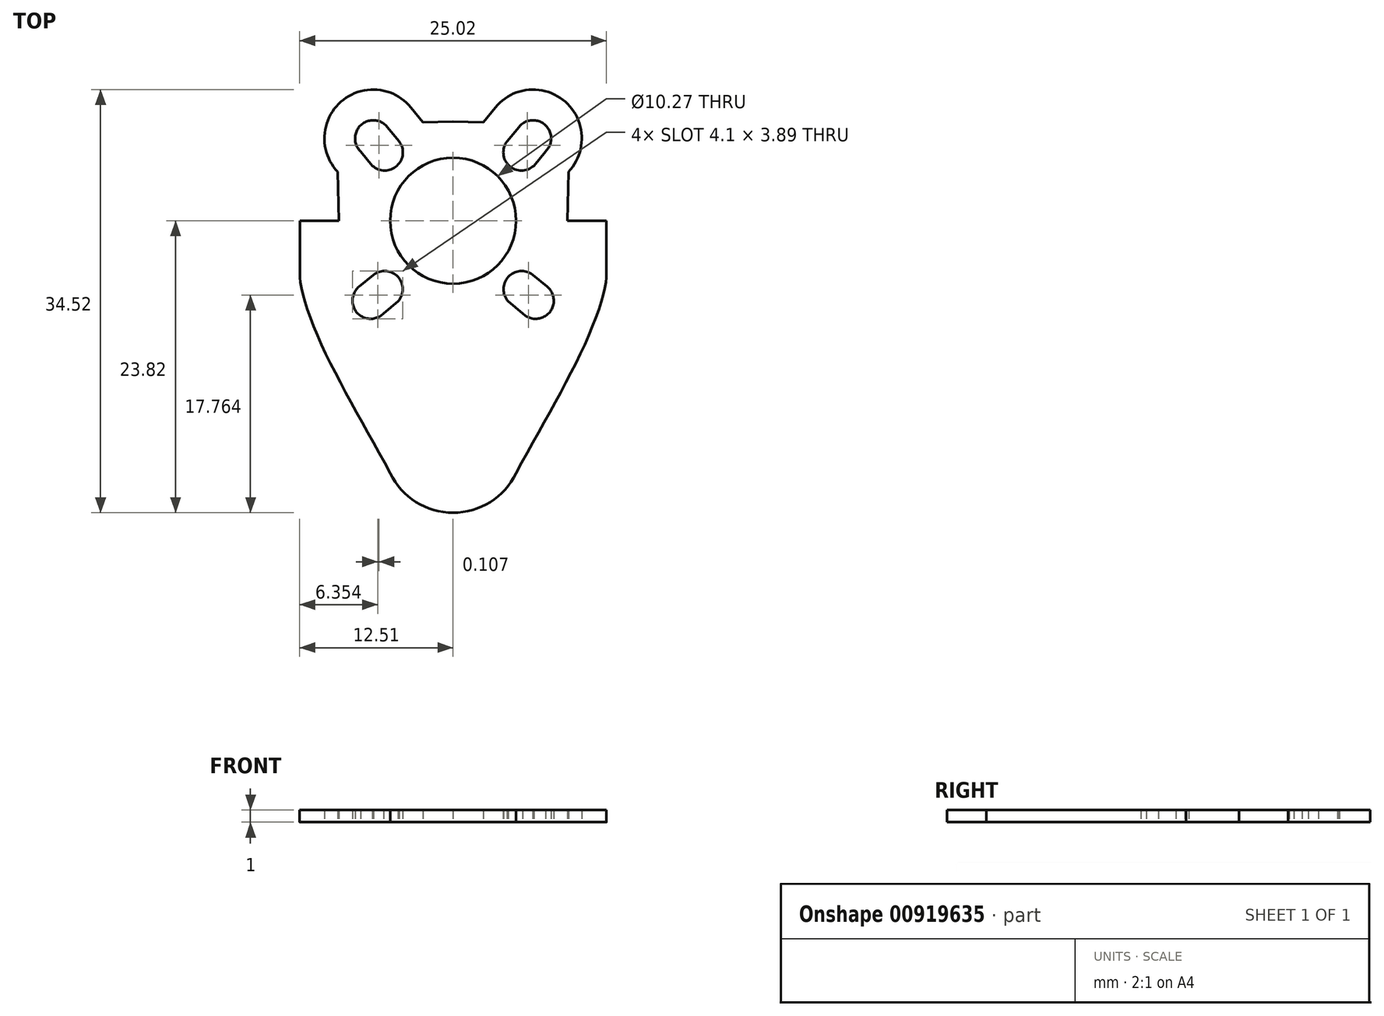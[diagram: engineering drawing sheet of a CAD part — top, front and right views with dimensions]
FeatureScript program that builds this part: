
annotation { "Feature Type Name" : "Feature", "Feature Type Description" : "" }
export const myFeature = defineFeature(function(context is Context, id is Id, definition is map)
    precondition{}
    {
        {
            var Q0;
            Q0=qCreatedBy(makeId("Top.planeOp"),FACE);
            var sketch = newSketch(context, id + "F0", { "sketchPlane" : qUnion([Q0])});
            skArc(sketch, "E0", {"start": v(-5.15, -20.56) * mm, "mid": v(-3.05, -22.94) * mm, "end": v(0, -23.82) * mm});
            skLineSegment(sketch, "E1.bottom", {"start": v(0, 0) * mm, "end": v(-12.5, 0) * mm});
            skLineSegment(sketch, "E1.right", {"start": v(-12.5, 0) * mm, "end": v(-12.5, -4.33) * mm});
            skPoint(sketch, "E1.middle", {"position": v(0, 0) * mm});
            skFitSpline(sketch, "E2", {"points": [v(-12.5, -4.33) * mm, v(-11.08, -9.31) * mm, v(-5.13, -20.6) * mm, v(-5.15, -20.56) * mm], "startDerivative": vector(-0.72, -6.32) * mm, "endDerivative": vector(-22.78, 42.97) * mm});
            skLineSegment(sketch, "E3", {"start": v(0, 0) * mm, "end": v(0, -23.82) * mm});
            skArc(sketch, "E4", {"start": v(-4.5, -6.58) * mm, "mid": v(-4.5, -4.58) * mm, "end": v(-6.49, -4.41) * mm});
            skArc(sketch, "E5", {"start": v(-7.67, -5.38) * mm, "mid": v(-7.82, -7.53) * mm, "end": v(-5.67, -7.55) * mm});
            skLineSegment(sketch, "E6", {"start": v(-6.49, -4.41) * mm, "end": v(-7.67, -5.38) * mm});
            skLineSegment(sketch, "E7", {"start": v(-5.67, -7.55) * mm, "end": v(-4.5, -6.58) * mm});
            skLineSegment(sketch, "E8.0", {"start": v(-14.38, 0) * mm, "end": v(-14.38, -4.33) * mm});
            skArc(sketch, "E9", {"start": v(-6.58, 4.49) * mm, "mid": v(-4.58, 4.49) * mm, "end": v(-4.4, 6.48) * mm});
            skArc(sketch, "E10", {"start": v(-5.37, 7.66) * mm, "mid": v(-7.52, 7.8) * mm, "end": v(-7.55, 5.66) * mm});
            skLineSegment(sketch, "E11", {"start": v(-4.4, 6.48) * mm, "end": v(-5.37, 7.66) * mm});
            skLineSegment(sketch, "E12", {"start": v(-7.55, 5.66) * mm, "end": v(-6.58, 4.49) * mm});
            skLineSegment(sketch, "E13.0", {"start": v(-2.45, 8.04) * mm, "end": v(-3.44, 9.25) * mm});
            skArc(sketch, "E13.1", {"start": v(-8.42, 2.79) * mm, "mid": v(-2.95, 2.59) * mm, "end": v(-2.45, 8.04) * mm});
            skLineSegment(sketch, "E13.2", {"start": v(-9.4, 3.98) * mm, "end": v(-8.42, 2.79) * mm});
            skArc(sketch, "E13.3", {"start": v(-3.44, 9.25) * mm, "mid": v(-9.15, 9.7) * mm, "end": v(-9.4, 3.98) * mm});
            skLineSegment(sketch, "E14.0", {"start": v(-8.05, -2.46) * mm, "end": v(-9.26, -3.45) * mm});
            skArc(sketch, "E14.1", {"start": v(-2.8, -8.42) * mm, "mid": v(-2.6, -2.95) * mm, "end": v(-8.05, -2.46) * mm});
            skLineSegment(sketch, "E14.2", {"start": v(-4, -9.41) * mm, "end": v(-2.8, -8.42) * mm});
            skArc(sketch, "E14.3", {"start": v(-9.26, -3.45) * mm, "mid": v(-9.71, -9.16) * mm, "end": v(-4, -9.41) * mm});
            skLineSegment(sketch, "E15", {"start": v(-9.4, 3.98) * mm, "end": v(-9.26, -3.45) * mm});
            skLineSegment(sketch, "E16", {"start": v(-2.45, 8.04) * mm, "end": v(0, 8.1) * mm});
            skLineSegment(sketch, "E17", {"start": v(0, 8.1) * mm, "end": v(0, 0) * mm});
            skLineSegment(sketch, "E18", {"start": v(0, 0) * mm, "end": v(0, -2.58) * mm});
            skCircle(sketch, "E19", {"center": v(0, 0) * mm, "radius": 5.13 * mm});
            skSolve(sketch);
        }
        {
            var Q0;
            {var subQ0=sQuery(id+"F0.wireOp",EDGE,"E2");var subQ1=sQuery(id+"F0.wireOp",EDGE,"E0");var subQ2=makeQuery(id+"F0.imprint","INTERSECT",VERTEX,{"disambiguationData":[OD(0.0)],"derivedFrom":[subQ1,subQ0]});Q0=makeQuery(id+"F0.imprint","IMPRINT",FACE,{"disambiguationData":[TD([[makeQuery(id+"F0.imprint","IMPRINT",EDGE,{"disambiguationData":[TD([[subQ2,-1.0]])],"derivedFrom":subQ1}),1.0]])]});}
            var Q1;
            {var subQ0=sQuery(id+"F0.wireOp",EDGE,"E16");Q1=makeQuery(id+"F0.imprint","IMPRINT",FACE,{"disambiguationData":[TD([[makeQuery(id+"F0.imprint","IMPRINT",EDGE,{"derivedFrom":subQ0}),-1.0]])]});}
            var Q2;
            {var subQ0=sQuery(id+"F0.wireOp",EDGE,"E13.2");Q2=makeQuery(id+"F0.imprint","IMPRINT",FACE,{"disambiguationData":[TD([[makeQuery(id+"F0.imprint","IMPRINT",EDGE,{"derivedFrom":subQ0}),-1.0]])]});}
            var Q3;
            {var subQ8=sQuery(id+"F0.wireOp",EDGE,"E1.right");Q3=makeQuery(id+"F0.imprint","IMPRINT",FACE,{"disambiguationData":[TD([[makeQuery(id+"F0.imprint","IMPRINT",EDGE,{"derivedFrom":subQ8}),1.0]])]});}
            var Q4;
            Q4=makeQuery(id+"F0.imprint","IMPRINT",FACE,{"disambiguationData":[TD([[makeQuery(id+"F0.imprint","IMPRINT",EDGE,{"derivedFrom":sQuery(id+"F0.wireOp",EDGE,"E9")}),-1.0]])]});
            var Q5;
            Q5=makeQuery(id+"F0.imprint","IMPRINT",FACE,{"disambiguationData":[TD([[makeQuery(id+"F0.imprint","IMPRINT",EDGE,{"derivedFrom":sQuery(id+"F0.wireOp",EDGE,"E4")}),-1.0]])]});
            var Q6;
            {var subQ1=sQuery(id+"F0.wireOp",EDGE,"E14.0");Q6=makeQuery(id+"F0.imprint","IMPRINT",FACE,{"disambiguationData":[TD([[makeQuery(id+"F0.imprint","IMPRINT",EDGE,{"derivedFrom":subQ1}),-1.0]])]});}
            extrude(context, id + "F1", {"entities" : qUnion([Q0, Q1, Q2, Q3, Q4, Q5, Q6]), "depth" : 1 * mm, "offsetDistance" : 25 * mm});
        }
        {
            var Q0;
            Q0=makeQuery(id+"F1.opExtrude","SWEPT_BODY",BODY,{"disambiguationData":[OSD([sQuery(id+"F0.wireOp",EDGE,"E0"),sQuery(id+"F0.wireOp",EDGE,"E1.bottom"),sQuery(id+"F0.wireOp",EDGE,"E1.right"),sQuery(id+"F0.wireOp",EDGE,"E2"),sQuery(id+"F0.wireOp",EDGE,"E3"),sQuery(id+"F0.wireOp",EDGE,"E4"),sQuery(id+"F0.wireOp",EDGE,"E5"),sQuery(id+"F0.wireOp",EDGE,"E6"),sQuery(id+"F0.wireOp",EDGE,"E7")])]});
            var Q1;
            Q1=qCreatedBy(makeId("Right.planeOp"),FACE);
            mirror(context, id + "F2", {"operationType" : NewBodyOperationType.ADD, "entities" : qUnion([Q0]), "mirrorPlane" : qUnion([Q1])});
        }
    });
